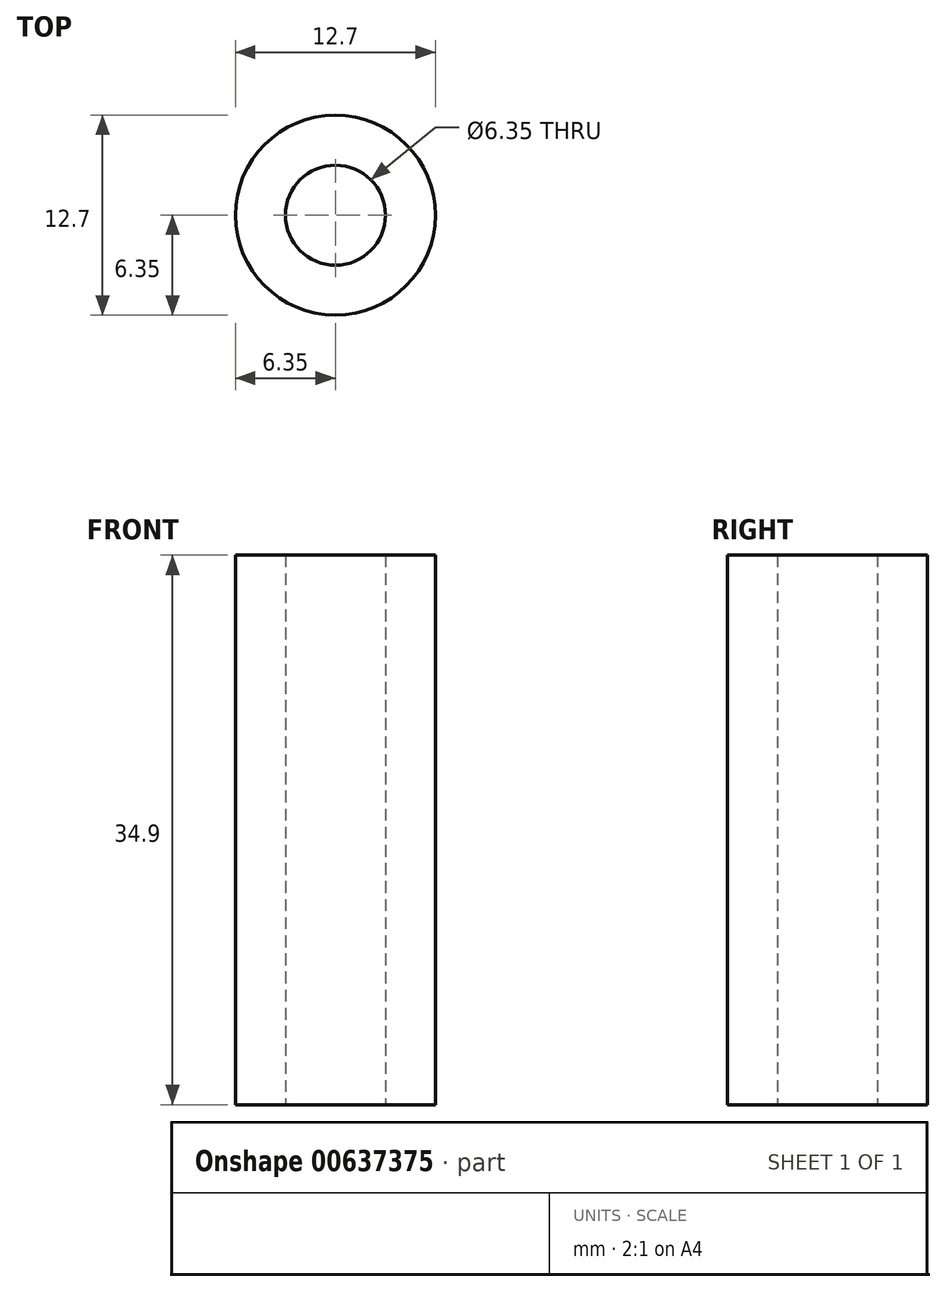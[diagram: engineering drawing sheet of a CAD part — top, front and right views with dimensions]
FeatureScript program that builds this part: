
annotation { "Feature Type Name" : "Feature", "Feature Type Description" : "" }
export const myFeature = defineFeature(function(context is Context, id is Id, definition is map)
    precondition{}
    {
        {
            var Q0;
            Q0=qCreatedBy(makeId("Top.planeOp"),FACE);
            var sketch = newSketch(context, id + "F0", { "sketchPlane" : qUnion([Q0])});
            skCircle(sketch, "E0", {"center": v(0, 0) * mm, "radius": 6.35 * mm});
            skCircle(sketch, "E1", {"center": v(0, 0) * mm, "radius": 3.17 * mm});
            skSolve(sketch);
        }
        {
            var Q0;
            Q0=makeQuery(id+"F0.imprint","IMPRINT",FACE,{"disambiguationData":[TD([[makeQuery(id+"F0.imprint","IMPRINT",EDGE,{"derivedFrom":sQuery(id+"F0.wireOp",EDGE,"E0")}),1.0]])]});
            extrude(context, id + "F1", {"entities" : qUnion([Q0]), "depth" : 34.9 * mm, "offsetDistance" : 25.4 * mm});
        }
    });
